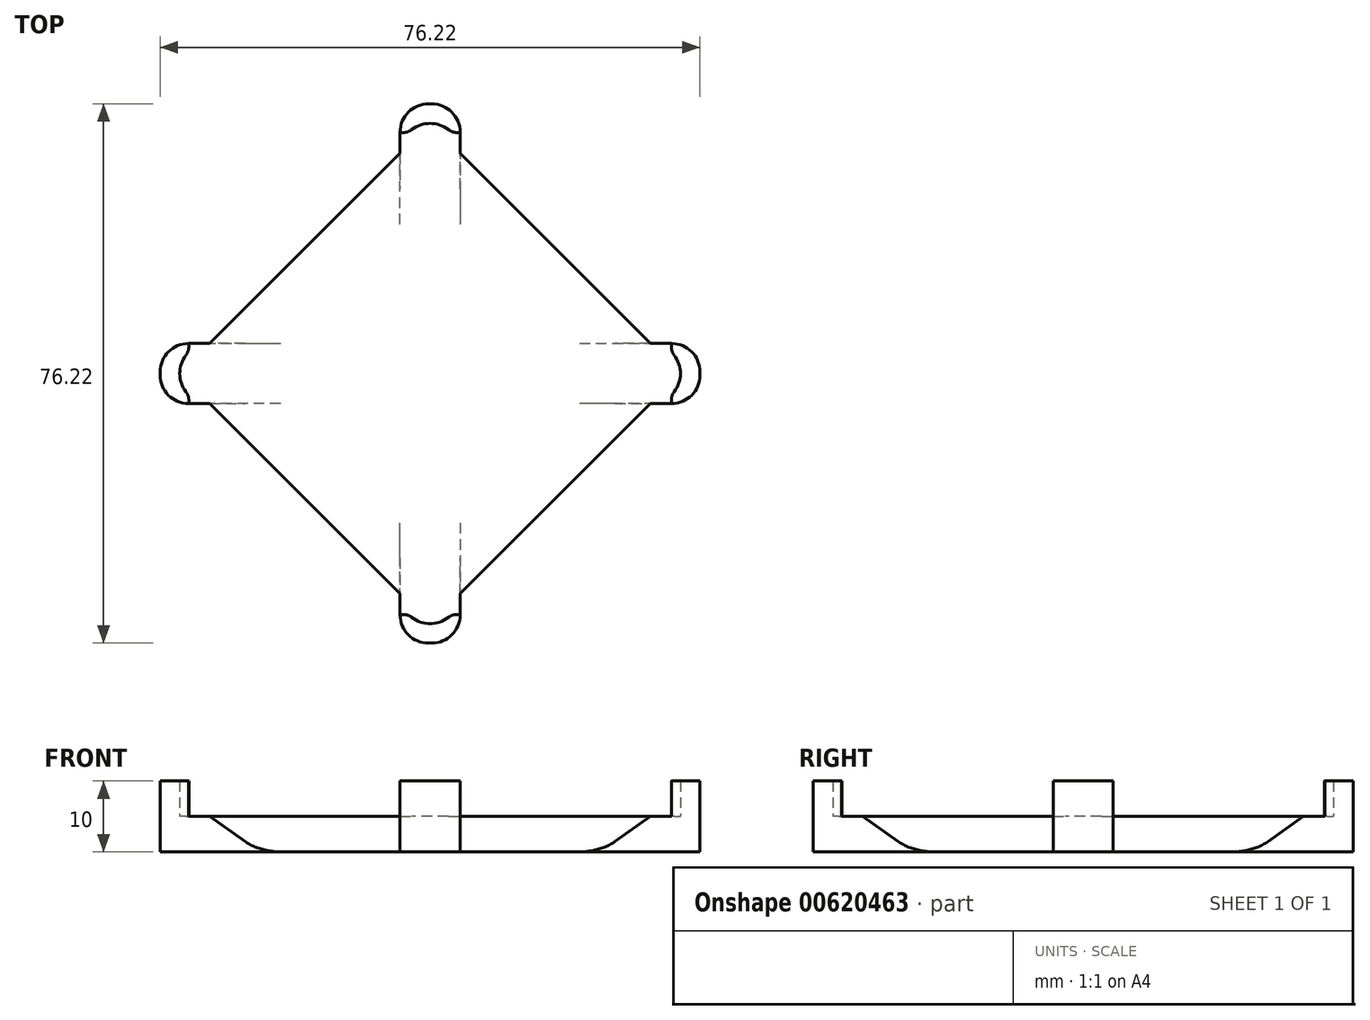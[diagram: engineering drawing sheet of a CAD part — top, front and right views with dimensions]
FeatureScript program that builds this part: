
annotation { "Feature Type Name" : "Feature", "Feature Type Description" : "" }
export const myFeature = defineFeature(function(context is Context, id is Id, definition is map)
    precondition{}
    {
        {
            var Q0;
            Q0=qCreatedBy(makeId("Top.planeOp"),FACE);
            var sketch = newSketch(context, id + "F0", { "sketchPlane" : qUnion([Q0])});
            skLineSegment(sketch, "E0", {"start": v(0, 35.36) * mm, "end": v(0, -35.36) * mm, "construction": true});
            skLineSegment(sketch, "E1", {"start": v(-35.36, 0) * mm, "end": v(35.36, 0) * mm, "construction": true});
            skPoint(sketch, "E2", {"position": v(0, 27.5) * mm});
            skPoint(sketch, "E3", {"position": v(-27.5, 0) * mm});
            skPoint(sketch, "E4", {"position": v(0, -27.5) * mm});
            skPoint(sketch, "E5", {"position": v(27.5, 0) * mm});
            skPoint(sketch, "E6", {"position": v(0, 0) * mm});
            skPoint(sketch, "E7", {"position": v(4.24, 31.11) * mm});
            skPoint(sketch, "E8", {"position": v(-4.24, 31.11) * mm});
            skPoint(sketch, "E9", {"position": v(-8.56, 26.8) * mm});
            skPoint(sketch, "E10", {"position": v(8.56, 26.8) * mm});
            skPoint(sketch, "E11", {"position": v(31.11, 4.24) * mm});
            skPoint(sketch, "E12", {"position": v(31.11, -4.24) * mm});
            skPoint(sketch, "E13", {"position": v(26.8, 8.56) * mm});
            skPoint(sketch, "E14", {"position": v(-31.11, -4.24) * mm});
            skPoint(sketch, "E15", {"position": v(-31.11, 4.24) * mm});
            skPoint(sketch, "E16", {"position": v(-26.8, 8.56) * mm});
            skPoint(sketch, "E17", {"position": v(4.24, -31.11) * mm});
            skPoint(sketch, "E18", {"position": v(-4.24, -31.11) * mm});
            skLineSegment(sketch, "E19", {"start": v(-31.11, 4.24) * mm, "end": v(-4.24, 31.11) * mm});
            skLineSegment(sketch, "E20", {"start": v(4.24, 31.11) * mm, "end": v(31.11, 4.24) * mm});
            skLineSegment(sketch, "E21", {"start": v(31.11, -4.24) * mm, "end": v(4.24, -31.11) * mm});
            skLineSegment(sketch, "E22", {"start": v(-4.24, -31.11) * mm, "end": v(-31.11, -4.24) * mm});
            skPoint(sketch, "E23", {"position": v(-17.68, -17.68) * mm});
            skPoint(sketch, "E24", {"position": v(17.68, -17.68) * mm});
            skPoint(sketch, "E25", {"position": v(17.68, 17.68) * mm});
            skPoint(sketch, "E26", {"position": v(-17.68, 17.68) * mm});
            skLineSegment(sketch, "E27", {"start": v(31.11, 4.24) * mm, "end": v(38.11, 4.24) * mm});
            skLineSegment(sketch, "E28", {"start": v(38.11, 4.24) * mm, "end": v(38.11, -4.24) * mm});
            skLineSegment(sketch, "E29", {"start": v(38.11, -4.24) * mm, "end": v(31.11, -4.24) * mm});
            skLineSegment(sketch, "E30", {"start": v(4.24, -31.11) * mm, "end": v(4.24, -38.11) * mm});
            skLineSegment(sketch, "E31", {"start": v(4.24, -38.11) * mm, "end": v(-4.24, -38.11) * mm});
            skLineSegment(sketch, "E32", {"start": v(-4.24, -38.11) * mm, "end": v(-4.24, -31.11) * mm});
            skLineSegment(sketch, "E33", {"start": v(-31.11, -4.24) * mm, "end": v(-38.11, -4.24) * mm});
            skLineSegment(sketch, "E34", {"start": v(-38.11, -4.24) * mm, "end": v(-38.11, 4.24) * mm});
            skLineSegment(sketch, "E35", {"start": v(-38.11, 4.24) * mm, "end": v(-31.11, 4.24) * mm});
            skLineSegment(sketch, "E36", {"start": v(-4.24, 31.11) * mm, "end": v(-4.24, 38.11) * mm});
            skLineSegment(sketch, "E37", {"start": v(-4.24, 38.11) * mm, "end": v(4.24, 38.11) * mm});
            skLineSegment(sketch, "E38", {"start": v(4.24, 38.11) * mm, "end": v(4.24, 31.11) * mm});
            skLineSegment(sketch, "E39", {"start": v(-4.24, -31.11) * mm, "end": v(4.24, -31.11) * mm});
            skLineSegment(sketch, "E40", {"start": v(31.11, -4.24) * mm, "end": v(31.11, 4.24) * mm});
            skLineSegment(sketch, "E41", {"start": v(4.24, 31.11) * mm, "end": v(-4.24, 31.11) * mm});
            skLineSegment(sketch, "E42", {"start": v(-31.11, 4.24) * mm, "end": v(-31.11, -4.24) * mm});
            skArc(sketch, "E43", {"start": v(-4.24, -31.11) * mm, "mid": v(0, -35.36) * mm, "end": v(4.24, -31.11) * mm});
            skArc(sketch, "E44", {"start": v(31.11, -4.24) * mm, "mid": v(35.36, 0) * mm, "end": v(31.11, 4.24) * mm});
            skArc(sketch, "E45", {"start": v(4.24, 31.11) * mm, "mid": v(0, 35.36) * mm, "end": v(-4.24, 31.11) * mm});
            skArc(sketch, "E46", {"start": v(-31.11, 4.24) * mm, "mid": v(-35.36, 0) * mm, "end": v(-31.11, -4.24) * mm});
            skSolve(sketch);
        }
        {
            var Q0;
            Q0=makeQuery(id+"F0.imprint","IMPRINT",FACE,{"disambiguationData":[TD([[makeQuery(id+"F0.imprint","IMPRINT",EDGE,{"derivedFrom":sQuery(id+"F0.wireOp",EDGE,"E39")}),-1.0]])]});
            var Q1;
            Q1=makeQuery(id+"F0.imprint","IMPRINT",FACE,{"disambiguationData":[TD([[makeQuery(id+"F0.imprint","IMPRINT",EDGE,{"derivedFrom":sQuery(id+"F0.wireOp",EDGE,"E19")}),-1.0]])]});
            var Q2;
            Q2=makeQuery(id+"F0.imprint","IMPRINT",FACE,{"disambiguationData":[TD([[makeQuery(id+"F0.imprint","IMPRINT",EDGE,{"derivedFrom":sQuery(id+"F0.wireOp",EDGE,"E42")}),-1.0]])]});
            var Q3;
            Q3=makeQuery(id+"F0.imprint","IMPRINT",FACE,{"disambiguationData":[TD([[makeQuery(id+"F0.imprint","IMPRINT",EDGE,{"derivedFrom":sQuery(id+"F0.wireOp",EDGE,"E40")}),-1.0]])]});
            var Q4;
            Q4=makeQuery(id+"F0.imprint","IMPRINT",FACE,{"disambiguationData":[TD([[makeQuery(id+"F0.imprint","IMPRINT",EDGE,{"derivedFrom":sQuery(id+"F0.wireOp",EDGE,"E27")}),-1.0]])]});
            var Q5;
            Q5=makeQuery(id+"F0.imprint","IMPRINT",FACE,{"disambiguationData":[TD([[makeQuery(id+"F0.imprint","IMPRINT",EDGE,{"derivedFrom":sQuery(id+"F0.wireOp",EDGE,"E30")}),-1.0]])]});
            var Q6;
            Q6=makeQuery(id+"F0.imprint","IMPRINT",FACE,{"disambiguationData":[TD([[makeQuery(id+"F0.imprint","IMPRINT",EDGE,{"derivedFrom":sQuery(id+"F0.wireOp",EDGE,"E33")}),-1.0]])]});
            var Q7;
            Q7=makeQuery(id+"F0.imprint","IMPRINT",FACE,{"disambiguationData":[TD([[makeQuery(id+"F0.imprint","IMPRINT",EDGE,{"derivedFrom":sQuery(id+"F0.wireOp",EDGE,"E41")}),-1.0]])]});
            var Q8;
            Q8=makeQuery(id+"F0.imprint","IMPRINT",FACE,{"disambiguationData":[TD([[makeQuery(id+"F0.imprint","IMPRINT",EDGE,{"derivedFrom":sQuery(id+"F0.wireOp",EDGE,"E36")}),-1.0]])]});
            extrude(context, id + "F1", {"entities" : qUnion([Q0, Q1, Q2, Q3, Q4, Q5, Q6, Q7, Q8]), "oppositeDirection" : true, "depth" : 5 * mm, "offsetDistance" : 25 * mm});
        }
        {
            var Q0;
            Q0=makeQuery(id+"F0.imprint","IMPRINT",FACE,{"disambiguationData":[TD([[makeQuery(id+"F0.imprint","IMPRINT",EDGE,{"derivedFrom":sQuery(id+"F0.wireOp",EDGE,"E33")}),-1.0]])]});
            var Q1;
            Q1=makeQuery(id+"F0.imprint","IMPRINT",FACE,{"disambiguationData":[TD([[makeQuery(id+"F0.imprint","IMPRINT",EDGE,{"derivedFrom":sQuery(id+"F0.wireOp",EDGE,"E30")}),-1.0]])]});
            var Q2;
            Q2=makeQuery(id+"F0.imprint","IMPRINT",FACE,{"disambiguationData":[TD([[makeQuery(id+"F0.imprint","IMPRINT",EDGE,{"derivedFrom":sQuery(id+"F0.wireOp",EDGE,"E36")}),-1.0]])]});
            var Q3;
            Q3=makeQuery(id+"F0.imprint","IMPRINT",FACE,{"disambiguationData":[TD([[makeQuery(id+"F0.imprint","IMPRINT",EDGE,{"derivedFrom":sQuery(id+"F0.wireOp",EDGE,"E27")}),-1.0]])]});
            extrude(context, id + "F2", {"entities" : qUnion([Q0, Q1, Q2, Q3]), "operationType" : NewBodyOperationType.ADD, "depth" : 5 * mm, "offsetDistance" : 25 * mm});
        }
        {
            var Q0;
            {var subQ0=sQuery(id+"F0.wireOp",EDGE,"E38");var subQ1=sQuery(id+"F0.wireOp",EDGE,"E37");Q0=makeQuery(id+"F2.boolean.opBoolean","MERGE",EDGE,{"derivedFrom":[makeQuery(id+"F1.opExtrude","SWEPT_EDGE",EDGE,{"disambiguationData":[OSD([subQ1,subQ0])]}),makeQuery(id+"F2.opExtrude","SWEPT_EDGE",EDGE,{"disambiguationData":[OSD([subQ1,subQ0])]})]});}
            var Q1;
            {var subQ0=sQuery(id+"F0.wireOp",EDGE,"E37");var subQ1=sQuery(id+"F0.wireOp",EDGE,"E36");Q1=makeQuery(id+"F2.boolean.opBoolean","MERGE",EDGE,{"derivedFrom":[makeQuery(id+"F1.opExtrude","SWEPT_EDGE",EDGE,{"disambiguationData":[OSD([subQ1,subQ0])]}),makeQuery(id+"F2.opExtrude","SWEPT_EDGE",EDGE,{"disambiguationData":[OSD([subQ1,subQ0])]})]});}
            var Q2;
            {var subQ0=sQuery(id+"F0.wireOp",EDGE,"E35");var subQ1=sQuery(id+"F0.wireOp",EDGE,"E34");Q2=makeQuery(id+"F2.boolean.opBoolean","MERGE",EDGE,{"derivedFrom":[makeQuery(id+"F1.opExtrude","SWEPT_EDGE",EDGE,{"disambiguationData":[OSD([subQ1,subQ0])]}),makeQuery(id+"F2.opExtrude","SWEPT_EDGE",EDGE,{"disambiguationData":[OSD([subQ1,subQ0])]})]});}
            var Q3;
            {var subQ0=sQuery(id+"F0.wireOp",EDGE,"E34");var subQ1=sQuery(id+"F0.wireOp",EDGE,"E33");Q3=makeQuery(id+"F2.boolean.opBoolean","MERGE",EDGE,{"derivedFrom":[makeQuery(id+"F1.opExtrude","SWEPT_EDGE",EDGE,{"disambiguationData":[OSD([subQ1,subQ0])]}),makeQuery(id+"F2.opExtrude","SWEPT_EDGE",EDGE,{"disambiguationData":[OSD([subQ1,subQ0])]})]});}
            var Q4;
            {var subQ0=sQuery(id+"F0.wireOp",EDGE,"E32");var subQ1=sQuery(id+"F0.wireOp",EDGE,"E31");Q4=makeQuery(id+"F2.boolean.opBoolean","MERGE",EDGE,{"derivedFrom":[makeQuery(id+"F1.opExtrude","SWEPT_EDGE",EDGE,{"disambiguationData":[OSD([subQ1,subQ0])]}),makeQuery(id+"F2.opExtrude","SWEPT_EDGE",EDGE,{"disambiguationData":[OSD([subQ1,subQ0])]})]});}
            var Q5;
            {var subQ0=sQuery(id+"F0.wireOp",EDGE,"E31");var subQ1=sQuery(id+"F0.wireOp",EDGE,"E30");Q5=makeQuery(id+"F2.boolean.opBoolean","MERGE",EDGE,{"derivedFrom":[makeQuery(id+"F1.opExtrude","SWEPT_EDGE",EDGE,{"disambiguationData":[OSD([subQ1,subQ0])]}),makeQuery(id+"F2.opExtrude","SWEPT_EDGE",EDGE,{"disambiguationData":[OSD([subQ1,subQ0])]})]});}
            var Q6;
            {var subQ0=sQuery(id+"F0.wireOp",EDGE,"E29");var subQ1=sQuery(id+"F0.wireOp",EDGE,"E28");Q6=makeQuery(id+"F2.boolean.opBoolean","MERGE",EDGE,{"derivedFrom":[makeQuery(id+"F1.opExtrude","SWEPT_EDGE",EDGE,{"disambiguationData":[OSD([subQ1,subQ0])]}),makeQuery(id+"F2.opExtrude","SWEPT_EDGE",EDGE,{"disambiguationData":[OSD([subQ1,subQ0])]})]});}
            var Q7;
            {var subQ0=sQuery(id+"F0.wireOp",EDGE,"E28");var subQ1=sQuery(id+"F0.wireOp",EDGE,"E27");Q7=makeQuery(id+"F2.boolean.opBoolean","MERGE",EDGE,{"derivedFrom":[makeQuery(id+"F1.opExtrude","SWEPT_EDGE",EDGE,{"disambiguationData":[OSD([subQ1,subQ0])]}),makeQuery(id+"F2.opExtrude","SWEPT_EDGE",EDGE,{"disambiguationData":[OSD([subQ1,subQ0])]})]});}
            fillet(context, id + "F3", {"entities" : qUnion([Q0, Q1, Q2, Q3, Q4, Q5, Q6, Q7]), "radius" : 4 * mm, "tangentPropagation" : true, "allowEdgeOverflow" : false});
        }
        {
            var Q0;
            Q0=makeQuery(id+"F2.opExtrude","SWEPT_EDGE",EDGE,{"disambiguationData":[OSD([sQuery(id+"F0.wireOp",EDGE,"E19"),sQuery(id+"F0.wireOp",EDGE,"E35"),sQuery(id+"F0.wireOp",EDGE,"E42"),sQuery(id+"F0.wireOp",EDGE,"E46")])]});
            var Q1;
            Q1=makeQuery(id+"F2.opExtrude","SWEPT_EDGE",EDGE,{"disambiguationData":[OSD([sQuery(id+"F0.wireOp",EDGE,"E22"),sQuery(id+"F0.wireOp",EDGE,"E33"),sQuery(id+"F0.wireOp",EDGE,"E42"),sQuery(id+"F0.wireOp",EDGE,"E46")])]});
            var Q2;
            Q2=makeQuery(id+"F2.opExtrude","SWEPT_EDGE",EDGE,{"disambiguationData":[OSD([sQuery(id+"F0.wireOp",EDGE,"E22"),sQuery(id+"F0.wireOp",EDGE,"E32"),sQuery(id+"F0.wireOp",EDGE,"E39"),sQuery(id+"F0.wireOp",EDGE,"E43")])]});
            var Q3;
            Q3=makeQuery(id+"F2.opExtrude","SWEPT_EDGE",EDGE,{"disambiguationData":[OSD([sQuery(id+"F0.wireOp",EDGE,"E21"),sQuery(id+"F0.wireOp",EDGE,"E30"),sQuery(id+"F0.wireOp",EDGE,"E39"),sQuery(id+"F0.wireOp",EDGE,"E43")])]});
            var Q4;
            Q4=makeQuery(id+"F2.opExtrude","SWEPT_EDGE",EDGE,{"disambiguationData":[OSD([sQuery(id+"F0.wireOp",EDGE,"E19"),sQuery(id+"F0.wireOp",EDGE,"E36"),sQuery(id+"F0.wireOp",EDGE,"E41"),sQuery(id+"F0.wireOp",EDGE,"E45")])]});
            var Q5;
            Q5=makeQuery(id+"F2.opExtrude","SWEPT_EDGE",EDGE,{"disambiguationData":[OSD([sQuery(id+"F0.wireOp",EDGE,"E20"),sQuery(id+"F0.wireOp",EDGE,"E38"),sQuery(id+"F0.wireOp",EDGE,"E41"),sQuery(id+"F0.wireOp",EDGE,"E45")])]});
            var Q6;
            Q6=makeQuery(id+"F2.opExtrude","SWEPT_EDGE",EDGE,{"disambiguationData":[OSD([sQuery(id+"F0.wireOp",EDGE,"E20"),sQuery(id+"F0.wireOp",EDGE,"E27"),sQuery(id+"F0.wireOp",EDGE,"E40"),sQuery(id+"F0.wireOp",EDGE,"E44")])]});
            var Q7;
            Q7=makeQuery(id+"F2.opExtrude","SWEPT_EDGE",EDGE,{"disambiguationData":[OSD([sQuery(id+"F0.wireOp",EDGE,"E21"),sQuery(id+"F0.wireOp",EDGE,"E29"),sQuery(id+"F0.wireOp",EDGE,"E40"),sQuery(id+"F0.wireOp",EDGE,"E44")])]});
            fillet(context, id + "F4", {"entities" : qUnion([Q0, Q1, Q2, Q3, Q4, Q5, Q6, Q7]), "radius" : 2 * mm, "tangentPropagation" : true, "allowEdgeOverflow" : false});
        }
        {
            var Q0;
            Q0=makeQuery(id+"F1.opExtrude","CAP_EDGE",EDGE,{"disambiguationData":[OSD([sQuery(id+"F0.wireOp",EDGE,"E19")])],"isStart":false});
            var Q1;
            Q1=makeQuery(id+"F1.opExtrude","CAP_EDGE",EDGE,{"disambiguationData":[OSD([sQuery(id+"F0.wireOp",EDGE,"E20")])],"isStart":false});
            var Q2;
            Q2=makeQuery(id+"F1.opExtrude","CAP_EDGE",EDGE,{"disambiguationData":[OSD([sQuery(id+"F0.wireOp",EDGE,"E21")])],"isStart":false});
            var Q3;
            Q3=makeQuery(id+"F1.opExtrude","CAP_EDGE",EDGE,{"disambiguationData":[OSD([sQuery(id+"F0.wireOp",EDGE,"E22")])],"isStart":false});
            chamfer(context, id + "F5", {"entities" : qUnion([Q0, Q1, Q2, Q3]), "width" : 5 * mm, "tangentPropagation" : true});
        }
        {
            var Q0;
            {var subQ0=sQuery(id+"F0.wireOp",EDGE,"E19");Q0=makeQuery(id+"F5.opChamfer","BLEND_EDGE",EDGE,{"blendedFrom":[makeQuery(id+"F1.opExtrude","CAP_EDGE",EDGE,{"disambiguationData":[OSD([subQ0])],"isStart":false}),makeQuery(id+"F1.opExtrude","CAP_FACE",FACE,{"disambiguationData":[OSD([subQ0,sQuery(id+"F0.wireOp",EDGE,"E20"),sQuery(id+"F0.wireOp",EDGE,"E21"),sQuery(id+"F0.wireOp",EDGE,"E22"),sQuery(id+"F0.wireOp",EDGE,"E27"),sQuery(id+"F0.wireOp",EDGE,"E28"),sQuery(id+"F0.wireOp",EDGE,"E29"),sQuery(id+"F0.wireOp",EDGE,"E30"),sQuery(id+"F0.wireOp",EDGE,"E31"),sQuery(id+"F0.wireOp",EDGE,"E32"),sQuery(id+"F0.wireOp",EDGE,"E33"),sQuery(id+"F0.wireOp",EDGE,"E34"),sQuery(id+"F0.wireOp",EDGE,"E35"),sQuery(id+"F0.wireOp",EDGE,"E36"),sQuery(id+"F0.wireOp",EDGE,"E37"),sQuery(id+"F0.wireOp",EDGE,"E38")])],"isStart":false})],"blendedInto":[makeQuery(id+"F1.opExtrude","CAP_FACE",FACE,{"disambiguationData":[OSD([subQ0,sQuery(id+"F0.wireOp",EDGE,"E20"),sQuery(id+"F0.wireOp",EDGE,"E21"),sQuery(id+"F0.wireOp",EDGE,"E22"),sQuery(id+"F0.wireOp",EDGE,"E27"),sQuery(id+"F0.wireOp",EDGE,"E28"),sQuery(id+"F0.wireOp",EDGE,"E29"),sQuery(id+"F0.wireOp",EDGE,"E30"),sQuery(id+"F0.wireOp",EDGE,"E31"),sQuery(id+"F0.wireOp",EDGE,"E32"),sQuery(id+"F0.wireOp",EDGE,"E33"),sQuery(id+"F0.wireOp",EDGE,"E34"),sQuery(id+"F0.wireOp",EDGE,"E35"),sQuery(id+"F0.wireOp",EDGE,"E36"),sQuery(id+"F0.wireOp",EDGE,"E37"),sQuery(id+"F0.wireOp",EDGE,"E38")])],"isStart":false})]});}
            var Q1;
            {var subQ0=sQuery(id+"F0.wireOp",EDGE,"E22");Q1=makeQuery(id+"F5.opChamfer","BLEND_EDGE",EDGE,{"blendedFrom":[makeQuery(id+"F1.opExtrude","CAP_EDGE",EDGE,{"disambiguationData":[OSD([subQ0])],"isStart":false}),makeQuery(id+"F1.opExtrude","CAP_FACE",FACE,{"disambiguationData":[OSD([sQuery(id+"F0.wireOp",EDGE,"E19"),sQuery(id+"F0.wireOp",EDGE,"E20"),sQuery(id+"F0.wireOp",EDGE,"E21"),subQ0,sQuery(id+"F0.wireOp",EDGE,"E27"),sQuery(id+"F0.wireOp",EDGE,"E28"),sQuery(id+"F0.wireOp",EDGE,"E29"),sQuery(id+"F0.wireOp",EDGE,"E30"),sQuery(id+"F0.wireOp",EDGE,"E31"),sQuery(id+"F0.wireOp",EDGE,"E32"),sQuery(id+"F0.wireOp",EDGE,"E33"),sQuery(id+"F0.wireOp",EDGE,"E34"),sQuery(id+"F0.wireOp",EDGE,"E35"),sQuery(id+"F0.wireOp",EDGE,"E36"),sQuery(id+"F0.wireOp",EDGE,"E37"),sQuery(id+"F0.wireOp",EDGE,"E38")])],"isStart":false})],"blendedInto":[makeQuery(id+"F1.opExtrude","CAP_FACE",FACE,{"disambiguationData":[OSD([sQuery(id+"F0.wireOp",EDGE,"E19"),sQuery(id+"F0.wireOp",EDGE,"E20"),sQuery(id+"F0.wireOp",EDGE,"E21"),subQ0,sQuery(id+"F0.wireOp",EDGE,"E27"),sQuery(id+"F0.wireOp",EDGE,"E28"),sQuery(id+"F0.wireOp",EDGE,"E29"),sQuery(id+"F0.wireOp",EDGE,"E30"),sQuery(id+"F0.wireOp",EDGE,"E31"),sQuery(id+"F0.wireOp",EDGE,"E32"),sQuery(id+"F0.wireOp",EDGE,"E33"),sQuery(id+"F0.wireOp",EDGE,"E34"),sQuery(id+"F0.wireOp",EDGE,"E35"),sQuery(id+"F0.wireOp",EDGE,"E36"),sQuery(id+"F0.wireOp",EDGE,"E37"),sQuery(id+"F0.wireOp",EDGE,"E38")])],"isStart":false})]});}
            var Q2;
            {var subQ0=sQuery(id+"F0.wireOp",EDGE,"E21");Q2=makeQuery(id+"F5.opChamfer","BLEND_EDGE",EDGE,{"blendedFrom":[makeQuery(id+"F1.opExtrude","CAP_EDGE",EDGE,{"disambiguationData":[OSD([subQ0])],"isStart":false}),makeQuery(id+"F1.opExtrude","CAP_FACE",FACE,{"disambiguationData":[OSD([sQuery(id+"F0.wireOp",EDGE,"E19"),sQuery(id+"F0.wireOp",EDGE,"E20"),subQ0,sQuery(id+"F0.wireOp",EDGE,"E22"),sQuery(id+"F0.wireOp",EDGE,"E27"),sQuery(id+"F0.wireOp",EDGE,"E28"),sQuery(id+"F0.wireOp",EDGE,"E29"),sQuery(id+"F0.wireOp",EDGE,"E30"),sQuery(id+"F0.wireOp",EDGE,"E31"),sQuery(id+"F0.wireOp",EDGE,"E32"),sQuery(id+"F0.wireOp",EDGE,"E33"),sQuery(id+"F0.wireOp",EDGE,"E34"),sQuery(id+"F0.wireOp",EDGE,"E35"),sQuery(id+"F0.wireOp",EDGE,"E36"),sQuery(id+"F0.wireOp",EDGE,"E37"),sQuery(id+"F0.wireOp",EDGE,"E38")])],"isStart":false})],"blendedInto":[makeQuery(id+"F1.opExtrude","CAP_FACE",FACE,{"disambiguationData":[OSD([sQuery(id+"F0.wireOp",EDGE,"E19"),sQuery(id+"F0.wireOp",EDGE,"E20"),subQ0,sQuery(id+"F0.wireOp",EDGE,"E22"),sQuery(id+"F0.wireOp",EDGE,"E27"),sQuery(id+"F0.wireOp",EDGE,"E28"),sQuery(id+"F0.wireOp",EDGE,"E29"),sQuery(id+"F0.wireOp",EDGE,"E30"),sQuery(id+"F0.wireOp",EDGE,"E31"),sQuery(id+"F0.wireOp",EDGE,"E32"),sQuery(id+"F0.wireOp",EDGE,"E33"),sQuery(id+"F0.wireOp",EDGE,"E34"),sQuery(id+"F0.wireOp",EDGE,"E35"),sQuery(id+"F0.wireOp",EDGE,"E36"),sQuery(id+"F0.wireOp",EDGE,"E37"),sQuery(id+"F0.wireOp",EDGE,"E38")])],"isStart":false})]});}
            var Q3;
            {var subQ0=sQuery(id+"F0.wireOp",EDGE,"E20");Q3=makeQuery(id+"F5.opChamfer","BLEND_EDGE",EDGE,{"blendedFrom":[makeQuery(id+"F1.opExtrude","CAP_EDGE",EDGE,{"disambiguationData":[OSD([subQ0])],"isStart":false}),makeQuery(id+"F1.opExtrude","CAP_FACE",FACE,{"disambiguationData":[OSD([sQuery(id+"F0.wireOp",EDGE,"E19"),subQ0,sQuery(id+"F0.wireOp",EDGE,"E21"),sQuery(id+"F0.wireOp",EDGE,"E22"),sQuery(id+"F0.wireOp",EDGE,"E27"),sQuery(id+"F0.wireOp",EDGE,"E28"),sQuery(id+"F0.wireOp",EDGE,"E29"),sQuery(id+"F0.wireOp",EDGE,"E30"),sQuery(id+"F0.wireOp",EDGE,"E31"),sQuery(id+"F0.wireOp",EDGE,"E32"),sQuery(id+"F0.wireOp",EDGE,"E33"),sQuery(id+"F0.wireOp",EDGE,"E34"),sQuery(id+"F0.wireOp",EDGE,"E35"),sQuery(id+"F0.wireOp",EDGE,"E36"),sQuery(id+"F0.wireOp",EDGE,"E37"),sQuery(id+"F0.wireOp",EDGE,"E38")])],"isStart":false})],"blendedInto":[makeQuery(id+"F1.opExtrude","CAP_FACE",FACE,{"disambiguationData":[OSD([sQuery(id+"F0.wireOp",EDGE,"E19"),subQ0,sQuery(id+"F0.wireOp",EDGE,"E21"),sQuery(id+"F0.wireOp",EDGE,"E22"),sQuery(id+"F0.wireOp",EDGE,"E27"),sQuery(id+"F0.wireOp",EDGE,"E28"),sQuery(id+"F0.wireOp",EDGE,"E29"),sQuery(id+"F0.wireOp",EDGE,"E30"),sQuery(id+"F0.wireOp",EDGE,"E31"),sQuery(id+"F0.wireOp",EDGE,"E32"),sQuery(id+"F0.wireOp",EDGE,"E33"),sQuery(id+"F0.wireOp",EDGE,"E34"),sQuery(id+"F0.wireOp",EDGE,"E35"),sQuery(id+"F0.wireOp",EDGE,"E36"),sQuery(id+"F0.wireOp",EDGE,"E37"),sQuery(id+"F0.wireOp",EDGE,"E38")])],"isStart":false})]});}
            fillet(context, id + "F6", {"entities" : qUnion([Q0, Q1, Q2, Q3]), "radius" : 5 * mm, "tangentPropagation" : true, "allowEdgeOverflow" : false});
        }
    });
